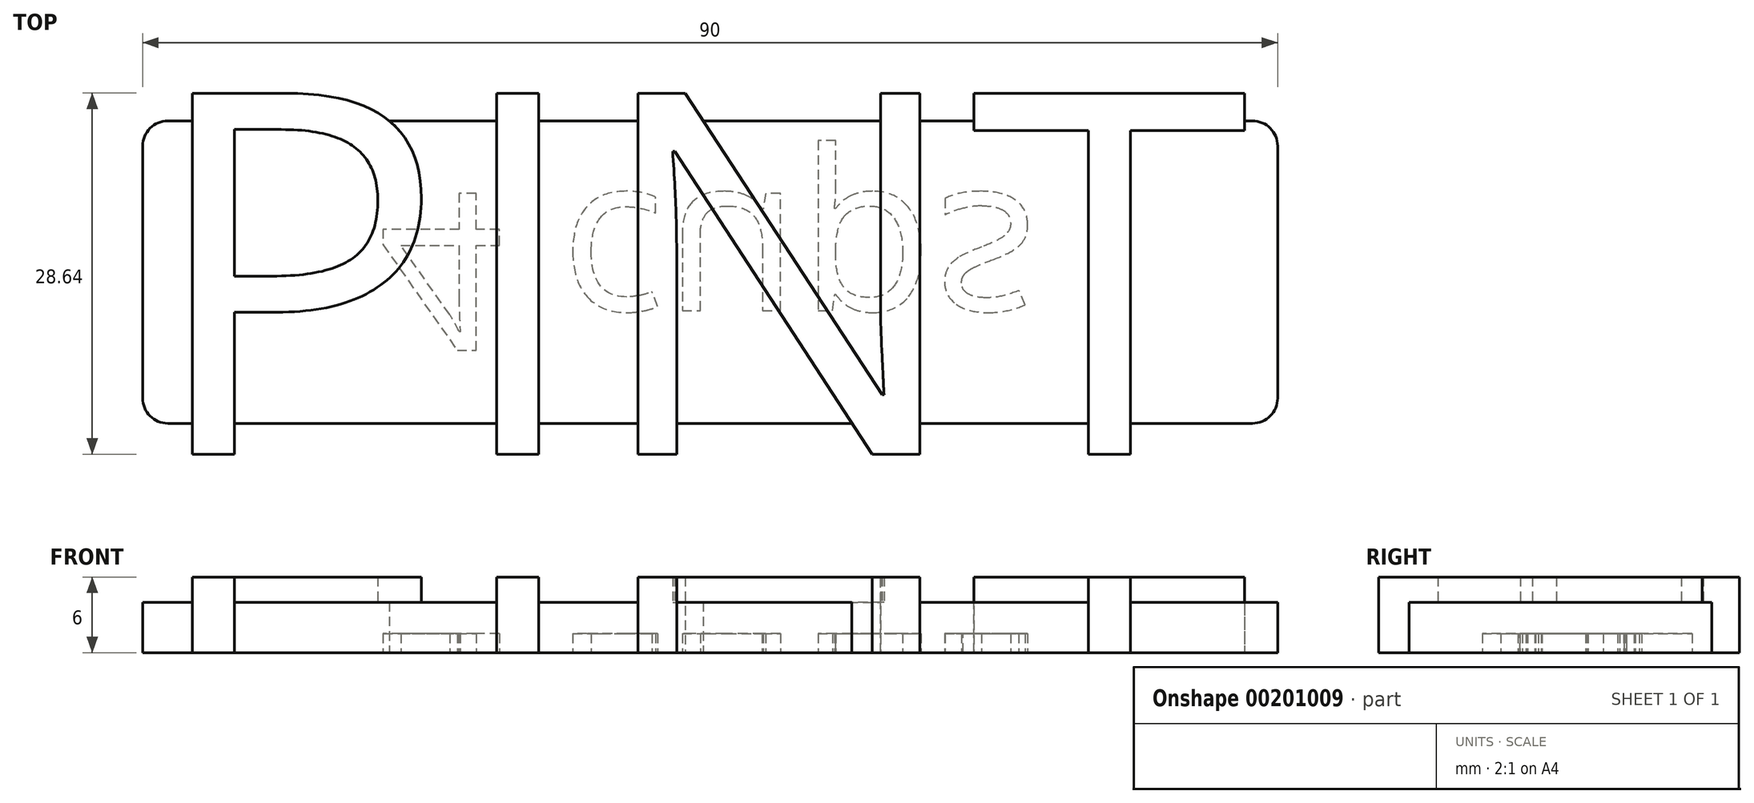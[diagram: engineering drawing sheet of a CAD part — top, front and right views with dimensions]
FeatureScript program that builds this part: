
annotation { "Feature Type Name" : "Feature", "Feature Type Description" : "" }
export const myFeature = defineFeature(function(context is Context, id is Id, definition is map)
    precondition{}
    {
        {
            var Q0;
            Q0=qCreatedBy(makeId("Top.planeOp"),FACE);
            var sketch = newSketch(context, id + "F0", { "sketchPlane" : qUnion([Q0])});
            skLineSegment(sketch, "E0.bottom", {"start": v(-45, 12) * mm, "end": v(45, 12) * mm});
            skLineSegment(sketch, "E0.top", {"start": v(-45, -12) * mm, "end": v(45, -12) * mm});
            skLineSegment(sketch, "E0.left", {"start": v(-45, 12) * mm, "end": v(-45, -12) * mm});
            skLineSegment(sketch, "E0.right", {"start": v(45, 12) * mm, "end": v(45, -12) * mm});
            skLineSegment(sketch, "E1", {"start": v(0, -12) * mm, "end": v(0, 12) * mm, "construction": true});
            skSolve(sketch);
        }
        {
            var Q0;
            Q0=makeQuery(id+"F0.imprint","IMPRINT",FACE,{"disambiguationData":[TD([[makeQuery(id+"F0.imprint","IMPRINT",EDGE,{"derivedFrom":sQuery(id+"F0.wireOp",EDGE,"E0.bottom")}),-1.0]])]});
            extrude(context, id + "F1", {"entities" : qUnion([Q0]), "depth" : 4 * mm});
        }
        {
            var Q0;
            Q0=makeQuery(id+"F1.opExtrude","SWEPT_EDGE",EDGE,{"disambiguationData":[OSD([sQuery(id+"F0.wireOp",EDGE,"E0.top"),sQuery(id+"F0.wireOp",EDGE,"E0.left")])]});
            var Q1;
            Q1=makeQuery(id+"F1.opExtrude","SWEPT_EDGE",EDGE,{"disambiguationData":[OSD([sQuery(id+"F0.wireOp",EDGE,"E0.bottom"),sQuery(id+"F0.wireOp",EDGE,"E0.right")])]});
            var Q2;
            Q2=makeQuery(id+"F1.opExtrude","SWEPT_EDGE",EDGE,{"disambiguationData":[OSD([sQuery(id+"F0.wireOp",EDGE,"E0.bottom"),sQuery(id+"F0.wireOp",EDGE,"E0.left")])]});
            var Q3;
            Q3=makeQuery(id+"F1.opExtrude","SWEPT_EDGE",EDGE,{"disambiguationData":[OSD([sQuery(id+"F0.wireOp",EDGE,"E0.top"),sQuery(id+"F0.wireOp",EDGE,"E0.right")])]});
            fillet(context, id + "F2", {"entities" : qUnion([Q0, Q1, Q2, Q3]), "radius" : 2 * mm, "tangentPropagation" : true, "allowEdgeOverflow" : false});
        }
        {
            var Q0;
            Q0=makeQuery(id+"F1.opExtrude","CAP_FACE",FACE,{"disambiguationData":[OSD([sQuery(id+"F0.wireOp",EDGE,"E0.bottom"),sQuery(id+"F0.wireOp",EDGE,"E0.top"),sQuery(id+"F0.wireOp",EDGE,"E0.left"),sQuery(id+"F0.wireOp",EDGE,"E0.right")])],"isStart":false});
            var sketch = newSketch(context, id + "F3", { "sketchPlane" : qUnion([Q0])});
            skText(sketch, "E2", { "text": "PINT", "fontName": "OpenSans-Regular.ttf"});
            const initialGuessF3  = {"E2": [-0.045, -0.01444, 1, 0, 0.02888]};
            skSetInitialGuess(sketch, initialGuessF3);
            skSolve(sketch);
        }
        {
            var Q0;
            {var subQ0=sQuery(id+"F3.wireOp",EDGE,"E2.sketch_text.stroke-4");Q0=makeQuery(id+"F3.imprint","IMPRINT",FACE,{"disambiguationData":[TD([[makeQuery(id+"F3.imprint","IMPRINT",EDGE,{"derivedFrom":subQ0}),-1.0]])]});}
            var Q1;
            {var subQ0=sQuery(id+"F3.wireOp",EDGE,"E2.sketch_text.stroke-3");var subQ1=sQuery(id+"F3.wireOp",EDGE,"E2.sketch_text.stroke-2");var subQ2=makeQuery(id+"F3.imprint","INTERSECT",VERTEX,{"derivedFrom":[subQ1,subQ0]});Q1=makeQuery(id+"F3.imprint","IMPRINT",FACE,{"disambiguationData":[TD([[makeQuery(id+"F3.imprint","IMPRINT",EDGE,{"disambiguationData":[TD([[subQ2,1.0]])],"derivedFrom":subQ1}),-1.0]])]});}
            var Q2;
            {var subQ1=sQuery(id+"F3.wireOp",EDGE,"E2.sketch_text.stroke-1");Q2=makeQuery(id+"F3.imprint","IMPRINT",FACE,{"disambiguationData":[TD([[makeQuery(id+"F3.imprint","IMPRINT",EDGE,{"derivedFrom":subQ1}),-1.0]])]});}
            var Q3;
            {var subQ0=sQuery(id+"F3.wireOp",EDGE,"E2.sketch_text.stroke-0");var subQ1=makeQuery(id+"F1.opExtrude","CAP_EDGE",EDGE,{"disambiguationData":[OSD([sQuery(id+"F0.wireOp",EDGE,"E0.top")])],"isStart":false});var subQ2=makeQuery(id+"F3.imprint","INTERSECT",VERTEX,{"derivedFrom":[subQ1,subQ0]});Q3=makeQuery(id+"F3.imprint","IMPRINT",FACE,{"disambiguationData":[TD([[makeQuery(id+"F3.imprint","IMPRINT",EDGE,{"disambiguationData":[TD([[subQ2,-1.0]])],"derivedFrom":subQ0}),-1.0]])]});}
            var Q4;
            {var subQ1=sQuery(id+"F3.wireOp",EDGE,"E2.sketch_text.stroke-8");Q4=makeQuery(id+"F3.imprint","IMPRINT",FACE,{"disambiguationData":[TD([[makeQuery(id+"F3.imprint","IMPRINT",EDGE,{"derivedFrom":subQ1}),-1.0]])]});}
            var Q5;
            {var subQ0=sQuery(id+"F3.wireOp",EDGE,"E2.sketch_text.stroke-9");var subQ1=makeQuery(id+"F1.opExtrude","CAP_EDGE",EDGE,{"disambiguationData":[OSD([sQuery(id+"F0.wireOp",EDGE,"E0.bottom")])],"isStart":false});var subQ2=makeQuery(id+"F3.imprint","INTERSECT",VERTEX,{"derivedFrom":[subQ1,subQ0]});Q5=makeQuery(id+"F3.imprint","IMPRINT",FACE,{"disambiguationData":[TD([[makeQuery(id+"F3.imprint","IMPRINT",EDGE,{"disambiguationData":[TD([[subQ2,1.0]])],"derivedFrom":subQ0}),-1.0]])]});}
            var Q6;
            {var subQ1=sQuery(id+"F3.wireOp",EDGE,"E2.sketch_text.stroke-10");Q6=makeQuery(id+"F3.imprint","IMPRINT",FACE,{"disambiguationData":[TD([[makeQuery(id+"F3.imprint","IMPRINT",EDGE,{"derivedFrom":subQ1}),-1.0]])]});}
            var Q7;
            {var subQ0=sQuery(id+"F3.wireOp",EDGE,"E2.sketch_text.stroke-11");var subQ1=makeQuery(id+"F1.opExtrude","CAP_EDGE",EDGE,{"disambiguationData":[OSD([sQuery(id+"F0.wireOp",EDGE,"E0.bottom")])],"isStart":false});var subQ2=makeQuery(id+"F3.imprint","INTERSECT",VERTEX,{"derivedFrom":[subQ1,subQ0]});Q7=makeQuery(id+"F3.imprint","IMPRINT",FACE,{"disambiguationData":[TD([[makeQuery(id+"F3.imprint","IMPRINT",EDGE,{"disambiguationData":[TD([[subQ2,-1.0]])],"derivedFrom":subQ0}),-1.0]])]});}
            var Q8;
            {var subQ0=sQuery(id+"F3.wireOp",EDGE,"E2.sketch_text.stroke-12");Q8=makeQuery(id+"F3.imprint","IMPRINT",FACE,{"disambiguationData":[TD([[makeQuery(id+"F3.imprint","IMPRINT",EDGE,{"derivedFrom":subQ0}),-1.0]])]});}
            var Q9;
            {var subQ0=sQuery(id+"F3.wireOp",EDGE,"E2.sketch_text.stroke-21");Q9=makeQuery(id+"F3.imprint","IMPRINT",FACE,{"disambiguationData":[TD([[makeQuery(id+"F3.imprint","IMPRINT",EDGE,{"derivedFrom":subQ0}),-1.0]])]});}
            var Q10;
            {var subQ0=sQuery(id+"F3.wireOp",EDGE,"E2.sketch_text.stroke-18");var subQ1=makeQuery(id+"F1.opExtrude","CAP_EDGE",EDGE,{"disambiguationData":[OSD([sQuery(id+"F0.wireOp",EDGE,"E0.top")])],"isStart":false});var subQ2=makeQuery(id+"F3.imprint","INTERSECT",VERTEX,{"derivedFrom":[subQ1,subQ0]});Q10=makeQuery(id+"F3.imprint","IMPRINT",FACE,{"disambiguationData":[TD([[makeQuery(id+"F3.imprint","IMPRINT",EDGE,{"disambiguationData":[TD([[subQ2,-1.0]])],"derivedFrom":subQ0}),-1.0]])]});}
            var Q11;
            {var subQ0=sQuery(id+"F3.wireOp",EDGE,"E2.sketch_text.stroke-19");Q11=makeQuery(id+"F3.imprint","IMPRINT",FACE,{"disambiguationData":[TD([[makeQuery(id+"F3.imprint","IMPRINT",EDGE,{"derivedFrom":subQ0}),-1.0]])]});}
            var Q12;
            {var subQ0=sQuery(id+"F3.wireOp",EDGE,"E2.sketch_text.stroke-25");Q12=makeQuery(id+"F3.imprint","IMPRINT",FACE,{"disambiguationData":[TD([[makeQuery(id+"F3.imprint","IMPRINT",EDGE,{"derivedFrom":subQ0}),-1.0]])]});}
            var Q13;
            {var subQ0=sQuery(id+"F3.wireOp",EDGE,"E2.sketch_text.stroke-22");var subQ1=makeQuery(id+"F1.opExtrude","CAP_EDGE",EDGE,{"disambiguationData":[OSD([sQuery(id+"F0.wireOp",EDGE,"E0.top")])],"isStart":false});var subQ2=makeQuery(id+"F3.imprint","INTERSECT",VERTEX,{"derivedFrom":[subQ1,subQ0]});Q13=makeQuery(id+"F3.imprint","IMPRINT",FACE,{"disambiguationData":[TD([[makeQuery(id+"F3.imprint","IMPRINT",EDGE,{"disambiguationData":[TD([[subQ2,-1.0]])],"derivedFrom":subQ0}),-1.0]])]});}
            var Q14;
            {var subQ0=sQuery(id+"F3.wireOp",EDGE,"E2.sketch_text.stroke-23");Q14=makeQuery(id+"F3.imprint","IMPRINT",FACE,{"disambiguationData":[TD([[makeQuery(id+"F3.imprint","IMPRINT",EDGE,{"derivedFrom":subQ0}),-1.0]])]});}
            var Q15;
            {var subQ5=sQuery(id+"F3.wireOp",EDGE,"E2.sketch_text.stroke-28");Q15=makeQuery(id+"F3.imprint","IMPRINT",FACE,{"disambiguationData":[TD([[makeQuery(id+"F3.imprint","IMPRINT",EDGE,{"derivedFrom":subQ5}),-1.0]])]});}
            var Q16;
            {var subQ0=sQuery(id+"F3.wireOp",EDGE,"E2.sketch_text.stroke-34");Q16=makeQuery(id+"F3.imprint","IMPRINT",FACE,{"disambiguationData":[TD([[makeQuery(id+"F3.imprint","IMPRINT",EDGE,{"derivedFrom":subQ0}),-1.0]])]});}
            var Q17;
            {var subQ0=sQuery(id+"F3.wireOp",EDGE,"E2.sketch_text.stroke-30");Q17=makeQuery(id+"F3.imprint","IMPRINT",FACE,{"disambiguationData":[TD([[makeQuery(id+"F3.imprint","IMPRINT",EDGE,{"derivedFrom":subQ0}),-1.0]])]});}
            var Q18;
            {var subQ0=sQuery(id+"F3.wireOp",EDGE,"E2.sketch_text.stroke-6");Q18=makeQuery(id+"F3.imprint","IMPRINT",FACE,{"disambiguationData":[TD([[makeQuery(id+"F3.imprint","IMPRINT",EDGE,{"derivedFrom":subQ0}),-1.0]])]});}
            var Q19;
            {var subQ0=sQuery(id+"F3.wireOp",EDGE,"E2.sketch_text.stroke-17");Q19=makeQuery(id+"F3.imprint","IMPRINT",FACE,{"disambiguationData":[TD([[makeQuery(id+"F3.imprint","IMPRINT",EDGE,{"derivedFrom":subQ0}),-1.0]])]});}
            var Q20;
            {var subQ0=sQuery(id+"F3.wireOp",EDGE,"E2.sketch_text.stroke-27");Q20=makeQuery(id+"F3.imprint","IMPRINT",FACE,{"disambiguationData":[TD([[makeQuery(id+"F3.imprint","IMPRINT",EDGE,{"derivedFrom":subQ0}),-1.0]])]});}
            var Q21;
            {var subQ0=sQuery(id+"F3.wireOp",EDGE,"E2.sketch_text.stroke-32");Q21=makeQuery(id+"F3.imprint","IMPRINT",FACE,{"disambiguationData":[TD([[makeQuery(id+"F3.imprint","IMPRINT",EDGE,{"derivedFrom":subQ0}),-1.0]])]});}
            var Q22;
            {var subQ5=sQuery(id+"F3.wireOp",EDGE,"E2.sketch_text.stroke-36");Q22=makeQuery(id+"F3.imprint","IMPRINT",FACE,{"disambiguationData":[TD([[makeQuery(id+"F3.imprint","IMPRINT",EDGE,{"derivedFrom":subQ5}),-1.0]])]});}
            var Q23;
            {var subQ0=sQuery(id+"F3.wireOp",EDGE,"E2.sketch_text.stroke-38");Q23=makeQuery(id+"F3.imprint","IMPRINT",FACE,{"disambiguationData":[TD([[makeQuery(id+"F3.imprint","IMPRINT",EDGE,{"derivedFrom":subQ0}),-1.0]])]});}
            extrude(context, id + "F4", {"entities" : qUnion([Q0, Q1, Q2, Q3, Q4, Q5, Q6, Q7, Q8, Q9, Q10, Q11, Q12, Q13, Q14, Q15, Q16, Q17, Q18, Q19, Q20, Q21, Q22, Q23]), "operationType" : NewBodyOperationType.ADD, "depth" : 2 * mm, "hasSecondDirection" : true, "secondDirectionOppositeDirection" : true, "secondDirectionDepth" : 4 * mm});
        }
        {
            var Q0;
            Q0=makeQuery(id+"F1.opExtrude","CAP_FACE",FACE,{"disambiguationData":[OSD([sQuery(id+"F0.wireOp",EDGE,"E0.bottom"),sQuery(id+"F0.wireOp",EDGE,"E0.top"),sQuery(id+"F0.wireOp",EDGE,"E0.left"),sQuery(id+"F0.wireOp",EDGE,"E0.right")])],"isStart":true});
            var sketch = newSketch(context, id + "F5", { "sketchPlane" : qUnion([Q0])});
            skText(sketch, "E3", { "text": "4 cups", "fontName": "OpenSans-Regular.ttf"});
            const initialGuessF5  = {"E3": [-0.0263, -0.00625, 1, 0, 0.0125]};
            skSetInitialGuess(sketch, initialGuessF5);
            skSolve(sketch);
        }
        {
            var Q0;
            Q0=makeQuery(id+"F5.imprint","IMPRINT",FACE,{"disambiguationData":[TD([[makeQuery(id+"F5.imprint","IMPRINT",EDGE,{"derivedFrom":sQuery(id+"F5.wireOp",EDGE,"E3.sketch_text.stroke-141")}),-1.0]])]});
            var Q1;
            Q1=makeQuery(id+"F5.imprint","IMPRINT",FACE,{"disambiguationData":[TD([[makeQuery(id+"F5.imprint","IMPRINT",EDGE,{"derivedFrom":sQuery(id+"F5.wireOp",EDGE,"E3.sketch_text.stroke-122")}),-1.0]])]});
            var Q2;
            Q2=makeQuery(id+"F5.imprint","IMPRINT",FACE,{"disambiguationData":[TD([[makeQuery(id+"F5.imprint","IMPRINT",EDGE,{"derivedFrom":sQuery(id+"F5.wireOp",EDGE,"E3.sketch_text.stroke-103")}),-1.0]])]});
            var Q3;
            Q3=makeQuery(id+"F5.imprint","IMPRINT",FACE,{"disambiguationData":[TD([[makeQuery(id+"F5.imprint","IMPRINT",EDGE,{"derivedFrom":sQuery(id+"F5.wireOp",EDGE,"E3.sketch_text.stroke-86")}),-1.0]])]});
            var Q4;
            Q4=makeQuery(id+"F5.imprint","IMPRINT",FACE,{"disambiguationData":[TD([[makeQuery(id+"F5.imprint","IMPRINT",EDGE,{"derivedFrom":sQuery(id+"F5.wireOp",EDGE,"E3.sketch_text.stroke-70")}),-1.0]])]});
            var Q5;
            Q5=makeQuery(id+"F5.imprint","IMPRINT",FACE,{"disambiguationData":[TD([[makeQuery(id+"F5.imprint","IMPRINT",EDGE,{"derivedFrom":sQuery(id+"F5.wireOp",EDGE,"E3.sketch_text.stroke-39")}),-1.0]])]});
            var Q6;
            Q6=makeQuery(id+"F5.imprint","IMPRINT",FACE,{"disambiguationData":[TD([[makeQuery(id+"F5.imprint","IMPRINT",EDGE,{"derivedFrom":sQuery(id+"F5.wireOp",EDGE,"E3.sketch_text.stroke-19")}),-1.0]])]});
            var Q7;
            Q7=makeQuery(id+"F5.imprint","IMPRINT",FACE,{"disambiguationData":[TD([[makeQuery(id+"F5.imprint","IMPRINT",EDGE,{"derivedFrom":sQuery(id+"F5.wireOp",EDGE,"E3.sketch_text.stroke-0")}),-1.0]])]});
            extrude(context, id + "F6", {"entities" : qUnion([Q0, Q1, Q2, Q3, Q4, Q5, Q6, Q7]), "operationType" : NewBodyOperationType.REMOVE, "oppositeDirection" : true, "depth" : 1.5 * mm});
        }
    });
